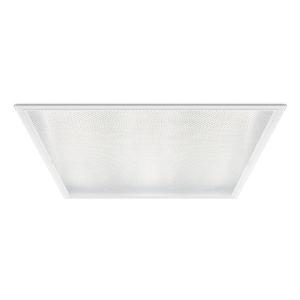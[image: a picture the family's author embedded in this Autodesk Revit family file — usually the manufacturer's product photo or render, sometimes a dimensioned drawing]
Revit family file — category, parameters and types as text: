
# Revit family: 3f_filippi_-_l_340_lite_sp_3f_filippi_-_23940_-_l_343x12w-940_sp_596x596
name_source: partatom
category: Lighting Fixtures
units: mm (PartAtom-declared; Revit-internal decimal feet)

## family parameters
Cut with Voids When Loaded = No
Host = Face
Light Source = No
Part Type = Normal
Room Calculation Point = No
Round Connector Dimension = Use Diameter
Shared = No

## types (1)
- 3F Filippi - L 340 Lite SP (1 x LED, 4255 lm, 43 W, 4000 K)
    Apparent Load = 43 VA
    Approval mark = ENEC
    CIE Flux Codes = 59 89 98 100 100
    Color Rendering = 90
    Color Temperature = 4000 K
    Control Gear = Electronic ballast
    Default Elevation = 1800 mm
    Description = ILLUMINOTECHNICAL
Luminous efficiency 100% (DLOR 100%, ULOR 0%).
Initial luminous flux of the luminaire 4255 lm.
Direct symmetric distribution.
Installation Interdistance Transv.D = 1.29 x hu - Long.D = 1.23 x hu.
Average luminance <3000 cd/m² for radial angles >65°.
Tabular UGR (CIE 117 - 4H-8H; S=0.25H; 70/50/20): RUG 18.5 - 18.2.
Beam angle: 96° - 93°.
Luminous efficacy 99 lm/W.
Lifetime (L93/B10): 30000 h. (tq+25°C)
Lifetime (L90/B10): 50000 h. (tq+25°C)
Lifetime (L85/B10): 80000 h. (tq+25°C)
Lifetime (L80/B10): 100000 h. (tq+25°C)
Sudden decreased luminous flux after 50000 hours: 0% (C0).
Photobiological safety in compliance with IEC/TR 62778: RG0 risk exempt, (IEC 62471).
In compliance with IEC/EN 62722-2-1 - IEC/EN 62717 standards.

SOURCE
3 squared LED modules 12W/940.
Energy efficiency class (UE 2019/2020 - UE 2019/2015): E.
CIE 13.3 Colour rendering index: CRI >90 (R9 >50%).
IES TM-30 Fidelity Index: Rf = 92 Rg = 101.
CCT nominal colour temperature 4000 K.
Colour initial tolerance (MacAdam): SDCM 3.

MECHANICAL
Housing in hot-galvanised steel, painted in white polyester.
Perimetral frame in white polycarbonate.
SP transparent methacrylate (PMMA) diffuser, prismatic outside, antiglare.
Luminaire with limited surface temperature. - D - (EN 60598-2-24)
Dimensions: 596x596 mm, height 80 mm. Weight 3.85 kg.
IP40 protection degree.
Mechanical strength to impacts IK06 (1 joule).
Glow-wire test resistance 650°C.

ELECTRICAL
Wiring on a separate unit.
Halogen Free electronic wiring 230V-50/60Hz, power factor 0.95, THD <25%, constant output current, SELV, class II, 1 driver.
Power of the luminaire 43 W.
CE - IEC 60598-1 - EN 60598-1.
SAFE FLICKER: PstLM=<1 and SVM=<0.4 (IEC TR 61547-1 and IEC TR 63158), to ensure a more comfortable and safe light.
Luminaire compliant with EN 60598-2-22 for power supply from a centralised emergency system CPSS (Central Power Supply System), not incorporated in the luminaire - high risk areas excluded. The default power and flux are 100% in AC and 100% in DC.
Ambient temperature from 0°C to +25°C.
Temperature class T6 max 85°C.
Relative humidity UR: <85%.

INSTALLATION
Lay-on or pull-up recessed fitting using frame accessory.
All accessories dedicated to this product are available on the Catalog and on our website www.3F-Filippi.com.

APPLICATIONS
Suitable product for food production plants (HACCP), IFS (Food Version 6), BRC (GSFS Food Version 7).
Environments: with VDTs, meeting rooms, offices.
Environments: architectural, commercial, staterooms, banks.
Environments where demanding visual tasks are performed and soft diffuse light is required for optimal visual comfort and total shielding of the light source.

WARNING
Luminaire designed for disposal/recycling at end-of-life.
Replaceable (LED only) light source by a professional. Replaceable control gear by a professional.
    Height = 0 mm  [stored 0 ft]
    Lamp = 1 x LED
    Lamp Light Flux = 4255 lm
    Lamp Power = 43 W
    Lamp count = 1
    Length = 596 mm
    Lifetime = 50000 h
    Luminous efficacy = 99 lm/W
    Manufacturer = 3F Filippi
    ModVariant = No
    Model = 3F Filippi - 23940 - L 343x12W-940 SP 596x596
    Mounting Place = Ceiling
    Mounting Type = Recessed
    Number of Poles = 1
    OnlyDefault = Yes
    Power Factor = 1
    Product Name = 3F Filippi - L 340 Lite SP
    Product group = recessed luminaire
    ProductGroupID = 4
    Protection Class = Protection class II
    Protection Degree = IP 40
    RLX_Detail_Level = 1
    RLX_Emergency_Light_Flux = 0 lm
    RLX_Emergency_Type = 0
    RLX_Emergency_Type_DB = No
    RlxData = <blob elided: 160493 chars, md5=df87d816>
    Socket = socket
    Standby Power = 0 W
    System Light Flux = 4255 lm
    System Power = 43 W
    Type Comments = Product without accessories
    Type Image = 3ffilippi_l_340_3x_sp.jpg
    URL = http://relux.com
    VarID = ---
    Voltage = 0 V
    Weight = 0.00 kg
    Width = 596 mm

note: [stored X ft] marks values corroborated as IEEE doubles in the binary element streams (Revit-internal decimal feet)

## geometry (parser evidence)
native form markers: Blend x4, Sweep x11
no freeform markers — native parametric forms only
